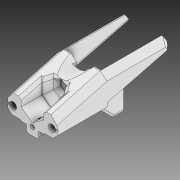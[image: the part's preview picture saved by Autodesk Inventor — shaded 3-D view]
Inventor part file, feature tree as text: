
AUTODESK INVENTOR PART (.ipt)
format: ipt  version: 2020 (Build 240168000, 168)  size: 298,496 bytes
history: native  units: in
note: dims shown in document units (in); Inventor stores cm internally (conversion verified against a paired STEP export)
features: extrude x4, sketch x4, fillet x1, chamfer x1, plane x1, imported_body x1
ambient origin geometry x8: Origin, YZ Plane, XZ Plane, XY Plane, X Axis, Y Axis, Z Axis, Center Point
bodies: Solid1 (feature_tree)
feature tree (12):
  extrude  "Extrusion1"  TaperAngle=0.0deg  [1 undecoded]
  fillet  "Fillet1"  Radius=0.0787in
  extrude  "Extrusion2"  Depth=0.0591in TaperAngle=45.0deg
  chamfer  "Chamfer1"  Distance=0.3937in
  extrude  "Extrusion3"  Depth=0.1181in
  plane  "Work Plane1"
  extrude  "Extrusion4"  Depth=0.2283in
  sketch  "Sketch1"  dims[d0=0.9843in d1=0.0in d2=0.0in d3=0.0787in]
  sketch  "Sketch2"  dims[d4=0.0in d5=0.0in d6=0.0591in d7=0.0787in d8=45.0deg]
  sketch  "Sketch3"  dims[d9=1.2598in]
  sketch  "Sketch4"  dims[d10=0.1378in d11=0.3937in d12=0.0in d13=0.1181in d14=0.2283in d15=0.2283in d16=0.1024in d17=0.0in]
  imported_body  "Base1"
note: 1 required parameter value undecoded (feature->parameter linkage not recoverable at this tier; creation-order binding heuristic only, values carry confidence <= 0.55)
